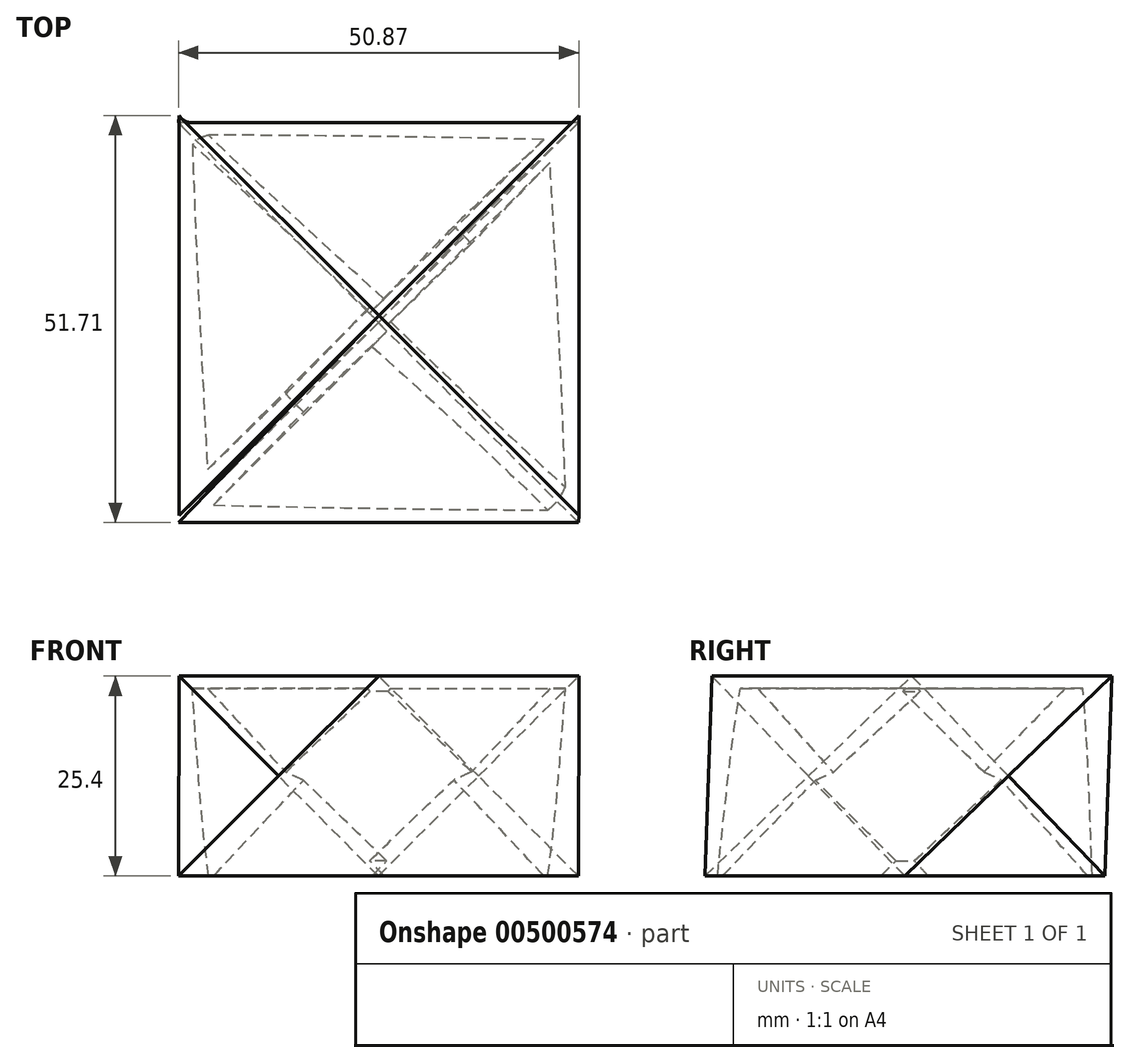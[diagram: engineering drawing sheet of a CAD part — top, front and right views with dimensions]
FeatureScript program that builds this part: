
annotation { "Feature Type Name" : "Feature", "Feature Type Description" : "" }
export const myFeature = defineFeature(function(context is Context, id is Id, definition is map)
    precondition{}
    {
        {
            var Q0;
            Q0=qCreatedBy(makeId("Top.planeOp"),FACE);
            var sketch = newSketch(context, id + "F0", { "sketchPlane" : qUnion([Q0])});
            skLineSegment(sketch, "E0.bottom", {"start": v(25.4, 25.4) * mm, "end": v(-25.4, 25.4) * mm});
            skLineSegment(sketch, "E0.top", {"start": v(25.4, -25.4) * mm, "end": v(-25.4, -25.4) * mm});
            skLineSegment(sketch, "E0.left", {"start": v(25.4, 25.4) * mm, "end": v(25.4, -25.4) * mm});
            skLineSegment(sketch, "E0.right", {"start": v(-25.4, 25.4) * mm, "end": v(-25.4, -25.4) * mm});
            skPoint(sketch, "E0.middle", {"position": v(0, 0) * mm});
            skLineSegment(sketch, "E1", {"start": v(-25.4, 25.4) * mm, "end": v(0, 0) * mm});
            skLineSegment(sketch, "E2", {"start": v(0, 0) * mm, "end": v(25.4, 25.4) * mm});
            skLineSegment(sketch, "E3", {"start": v(0, 0) * mm, "end": v(25.4, -25.4) * mm});
            skLineSegment(sketch, "E4", {"start": v(-25.4, -25.4) * mm, "end": v(0, 0) * mm});
            skSolve(sketch);
        }
        {
            var Q0;
            Q0=qCreatedBy(makeId("Top.planeOp"),FACE);
            cPlane(context, id + "F1", {"entities" : qUnion([Q0]), "cplaneType" : CPlaneType.OFFSET, "offset" : 25.4 * mm, "width" : 152.4 * mm, "height" : 152.4 * mm});
        }
        {
            var Q0;
            Q0=qCreatedBy(id+"F1.planeOp",FACE);
            var sketch = newSketch(context, id + "F2", { "sketchPlane" : qUnion([Q0])});
            skLineSegment(sketch, "E5.bottom", {"start": v(25.47, 26.31) * mm, "end": v(-25.33, 26.31) * mm});
            skLineSegment(sketch, "E5.top", {"start": v(25.47, -24.49) * mm, "end": v(-25.33, -24.49) * mm});
            skLineSegment(sketch, "E5.left", {"start": v(25.47, 26.31) * mm, "end": v(25.47, -24.49) * mm});
            skLineSegment(sketch, "E5.right", {"start": v(-25.33, 26.31) * mm, "end": v(-25.33, -24.49) * mm});
            skPoint(sketch, "E5.middle", {"position": v(0.07, 0.91) * mm});
            skLineSegment(sketch, "E6", {"start": v(-25.33, 26.31) * mm, "end": v(0.07, 0.91) * mm});
            skLineSegment(sketch, "E7", {"start": v(0.07, 0.91) * mm, "end": v(25.47, 26.31) * mm});
            skLineSegment(sketch, "E8", {"start": v(0.07, 0.91) * mm, "end": v(25.47, -24.49) * mm});
            skLineSegment(sketch, "E9", {"start": v(-25.33, -24.49) * mm, "end": v(0.07, 0.91) * mm});
            skSolve(sketch);
        }
        {
            var Q0;
            Q0=makeQuery(id+"F0.imprint","IMPRINT",FACE,{"disambiguationData":[TD([[makeQuery(id+"F0.imprint","IMPRINT",EDGE,{"derivedFrom":sQuery(id+"F0.wireOp",EDGE,"E0.top")}),-1.0]])]});
            var Q1;
            Q1=makeQuery(id+"F2.imprint","IMPRINT",FACE,{"disambiguationData":[TD([[makeQuery(id+"F2.imprint","IMPRINT",EDGE,{"derivedFrom":sQuery(id+"F2.wireOp",EDGE,"E5.left")}),-1.0]])]});
            loft(context, id + "F3", {"sheetProfilesArray" : [{ "sheetProfileEntities" : qUnion([Q0]) }, { "sheetProfileEntities" : qUnion([Q1]) }]});
        }
        {
            var Q1;
            Q1=makeQuery(id+"F0.imprint","IMPRINT",FACE,{"disambiguationData":[TD([[makeQuery(id+"F0.imprint","IMPRINT",EDGE,{"derivedFrom":sQuery(id+"F0.wireOp",EDGE,"E0.bottom")}),1.0]])]});
            var Q2;
            Q2=makeQuery(id+"F2.imprint","IMPRINT",FACE,{"disambiguationData":[TD([[makeQuery(id+"F2.imprint","IMPRINT",EDGE,{"derivedFrom":sQuery(id+"F2.wireOp",EDGE,"E5.right")}),1.0]])]});
            loft(context, id + "F4", {"operationType" : NewBodyOperationType.ADD, "sheetProfilesArray" : [{ "sheetProfileEntities" : qUnion([Q1]) }, { "sheetProfileEntities" : qUnion([Q2]) }]});
        }
        {
            var Q0;
            Q0=makeQuery(id+"F3.opLoft","CAP_FACE",FACE,{"disambiguationData":[OSD([makeQuery(id+"F0.imprint","IMPRINT",FACE,{"disambiguationData":[TD([[makeQuery(id+"F0.imprint","IMPRINT",EDGE,{"derivedFrom":sQuery(id+"F0.wireOp",EDGE,"E0.top")}),-1.0]])]})])],"isStart":true});
            var Q1;
            Q1=makeQuery(id+"F4.opLoft","CAP_FACE",FACE,{"disambiguationData":[OSD([makeQuery(id+"F0.imprint","IMPRINT",FACE,{"disambiguationData":[TD([[makeQuery(id+"F0.imprint","IMPRINT",EDGE,{"derivedFrom":sQuery(id+"F0.wireOp",EDGE,"E0.bottom")}),1.0]])]})])],"isStart":true});
            shell(context, id + "F5", {"entities" : qUnion([Q0, Q1]), "thickness" : 1.59 * mm});
        }
    });
